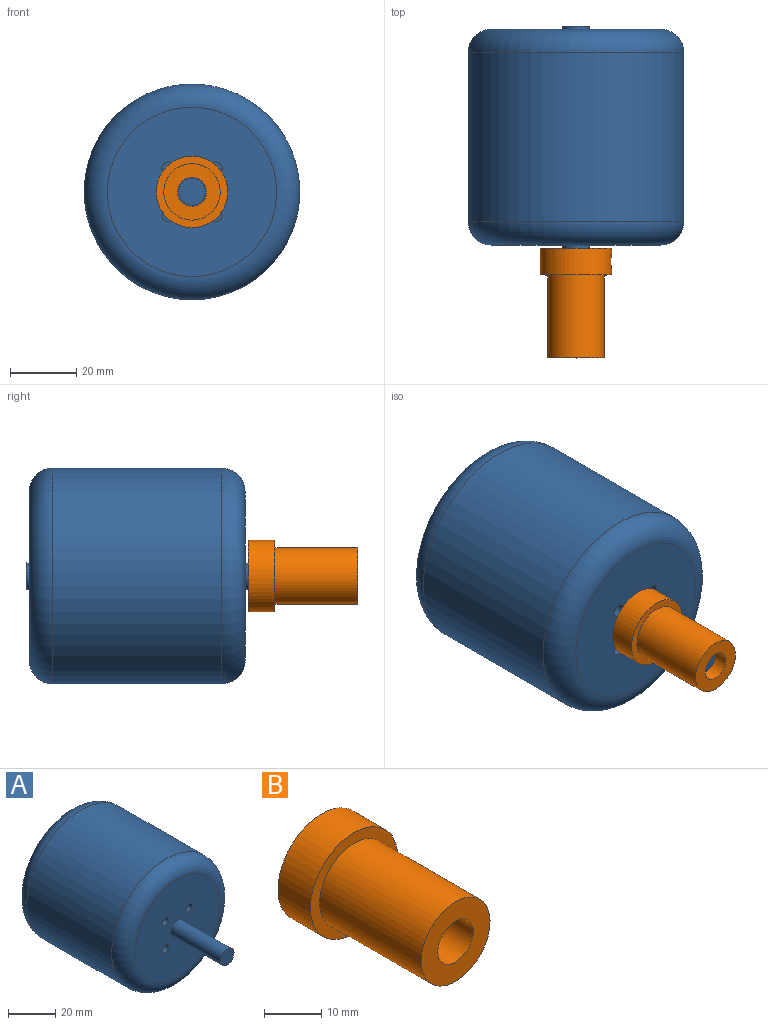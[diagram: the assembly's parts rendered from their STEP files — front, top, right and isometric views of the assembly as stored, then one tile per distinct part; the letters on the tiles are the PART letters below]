
ASSEMBLY  parts=2 mates=1
PART A: 17 faces, bbox 70.4x96x70.4 mm
  f0: cylinder r=32.5mm len=65mm, axis (0,-1,0), area 10414.4mm2, adj f15,f16
  f1: plane 51x51mm, normal (0,1,0), area 1992.6mm2, adj f5,f16
  f2: plane 51x51mm, normal (0,-1,0), area 1942.3mm2, adj f4,f7,f9,f11,f13,f15
  f3: plane 8x8mm, normal (0,-1,0), area 50.3mm2, adj f4
  f4: cylinder r=4mm len=30mm, axis (0,1,0), area 754mm2, adj f2,f3
  f5: cylinder r=4mm len=8mm, axis (0,1,0), area 25.1mm2, adj f1,f6
  f6: plane 8x8mm, normal (0,1,0), area 50.3mm2, adj f5
  f7: cylinder r=2mm len=10mm, axis (0,-1,0), area 125.7mm2, adj f2,f8
  f8: plane 4x4mm, normal (0,-1,0), area 12.6mm2, adj f7
  f9: cylinder r=2mm len=10mm, axis (0,-1,0), area 125.7mm2, adj f2,f10
  f10: plane 4x4mm, normal (0,-1,0), area 12.6mm2, adj f9
  f11: cylinder r=2mm len=10mm, axis (0,-1,0), area 125.7mm2, adj f2,f12
  f12: plane 4x4mm, normal (0,-1,0), area 12.6mm2, adj f11
  f13: cylinder r=2mm len=10mm, axis (0,-1,0), area 125.7mm2, adj f2,f14
  f14: plane 4x4mm, normal (0,-1,0), area 12.6mm2, adj f13
  f15: torus R=25.5mm, axis (0,-1,0), area 2069.6mm2, adj f0,f2
  f16: torus R=25.5mm, axis (0,-1,0), area 2069.6mm2, adj f0,f1
PART B: 7 faces, bbox 21.6x33x21.6 mm
  f0: cylinder r=4.38mm len=33mm, axis (0,1,0), area 886.9mm2, adj f3,f4,f6
  f1: cylinder r=10.78mm len=21.57mm, axis (0,1,0), area 522.2mm2, adj f2,f3,f4
  f2: plane 21.57x21.57mm, normal (0,-1,0), area 138.3mm2, adj f1,f5
  f3: plane 21.57x21.57mm, normal (0,1,0), area 305.1mm2, adj f0,f1
  f4: cylinder r=2.5mm len=7.19mm, axis (-1,0,0), area 104.3mm2, adj f0,f1
  f5: cylinder r=8.5mm len=25mm, axis (0,1,0), area 1335.2mm2, adj f2,f6
  f6: plane 17x17mm, normal (0,-1,0), area 166.8mm2, adj f0,f5
PLACE A t=(-3.58,-5.96,-11.05)mm
PLACE B t=(-3.58,-6.96,-11.05)mm
MATE fastened B.f1 <-> A.f0  axis (0,1,0) through (-3.58,-6.96,-11.05)mm
